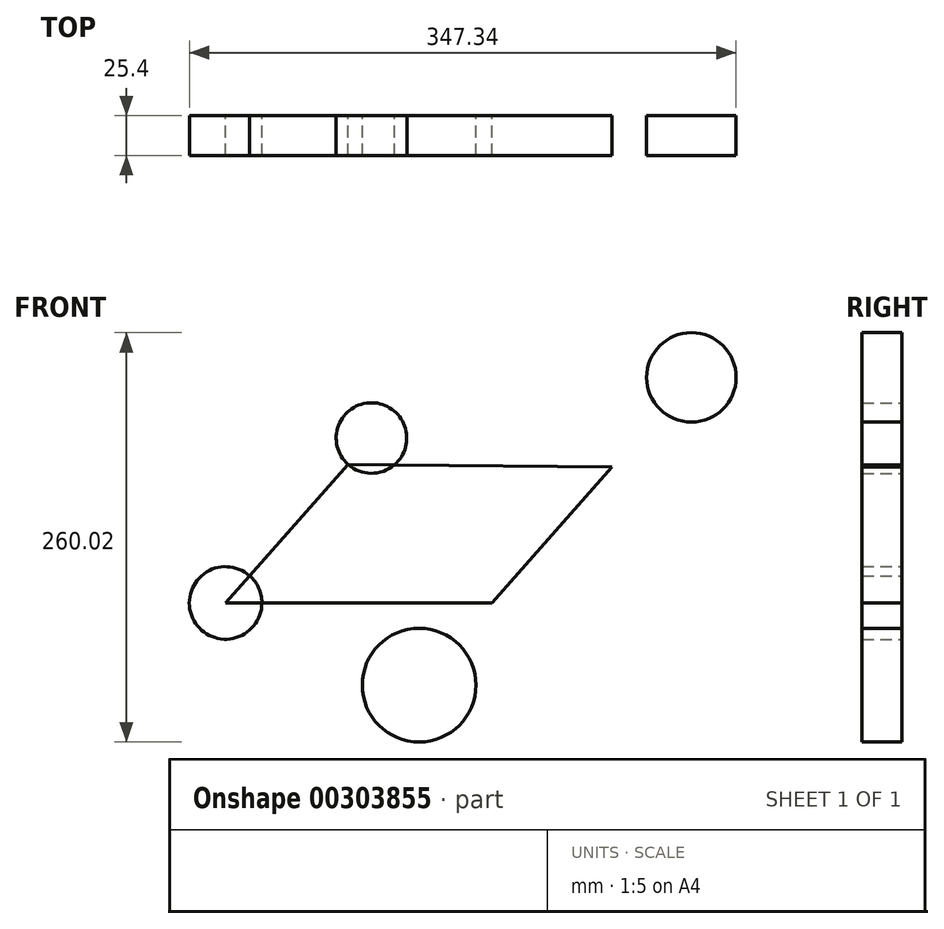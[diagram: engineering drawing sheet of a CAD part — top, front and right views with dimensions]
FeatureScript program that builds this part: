
annotation { "Feature Type Name" : "Feature", "Feature Type Description" : "" }
export const myFeature = defineFeature(function(context is Context, id is Id, definition is map)
    precondition{}
    {
        {
            var Q0;
            Q0=qCreatedBy(makeId("Front.planeOp"),FACE);
            var sketch = newSketch(context, id + "F0", { "sketchPlane" : qUnion([Q0])});
            skLineSegment(sketch, "E0", {"start": v(-129.95, -28.94) * mm, "end": v(-37.28, 75.8) * mm});
            skCircle(sketch, "E1", {"center": v(-37.28, 75.8) * mm, "radius": 22.41 * mm});
            skCircle(sketch, "E2", {"center": v(-129.95, -28.94) * mm, "radius": 23.04 * mm});
            skLineSegment(sketch, "E3", {"start": v(-129.95, -28.94) * mm, "end": v(39.16, -28.94) * mm});
            skLineSegment(sketch, "E4", {"start": v(39.16, -28.94) * mm, "end": v(115.44, 57.28) * mm});
            skLineSegment(sketch, "E5", {"start": v(115.44, 57.28) * mm, "end": v(-52.13, 59.02) * mm});
            skLineSegment(sketch, "E6", {"start": v(115.44, 57.28) * mm, "end": v(-7.02, -81.15) * mm});
            skLineSegment(sketch, "E7", {"start": v(-7.02, -81.15) * mm, "end": v(115.44, 57.28) * mm});
            skLineSegment(sketch, "E8", {"start": v(115.44, 57.28) * mm, "end": v(165.93, 114.35) * mm});
            skCircle(sketch, "E9", {"center": v(-7.02, -81.15) * mm, "radius": 36.1 * mm});
            skCircle(sketch, "E10", {"center": v(165.93, 114.35) * mm, "radius": 28.42 * mm});
            skSolve(sketch);
        }
        {
            var Q0;
            {var subQ0=sQuery(id+"F0.wireOp",EDGE,"E3");var subQ1=sQuery(id+"F0.wireOp",EDGE,"E0");var subQ2=makeQuery(id+"F0.imprint","INTERSECT",VERTEX,{"derivedFrom":[subQ1,subQ0]});Q0=makeQuery(id+"F0.imprint","IMPRINT",FACE,{"disambiguationData":[TD([[makeQuery(id+"F0.imprint","IMPRINT",EDGE,{"disambiguationData":[TD([[subQ2,-1.0]])],"derivedFrom":subQ1}),1.0]])]});}
            var Q1;
            Q1=makeQuery(id+"F0.imprint","IMPRINT",FACE,{"disambiguationData":[TD([[makeQuery(id+"F0.imprint","IMPRINT",EDGE,{"derivedFrom":sQuery(id+"F0.wireOp",EDGE,"E10")}),1.0]])]});
            var Q2;
            {var subQ0=sQuery(id+"F0.wireOp",EDGE,"E5");var subQ1=sQuery(id+"F0.wireOp",EDGE,"E1");var subQ3=makeQuery(id+"F0.imprint","INTERSECT",VERTEX,{"derivedFrom":[subQ1,subQ0]});Q2=makeQuery(id+"F0.imprint","IMPRINT",FACE,{"disambiguationData":[TD([[makeQuery(id+"F0.imprint","IMPRINT",EDGE,{"disambiguationData":[TD([[subQ3,-1.0]])],"derivedFrom":subQ1}),1.0]])]});}
            var Q3;
            {var subQ0=sQuery(id+"F0.wireOp",EDGE,"E2");var subQ1=sQuery(id+"F0.wireOp",EDGE,"E0");var subQ2=makeQuery(id+"F0.imprint","INTERSECT",VERTEX,{"derivedFrom":[subQ1,subQ0]});Q3=makeQuery(id+"F0.imprint","IMPRINT",FACE,{"disambiguationData":[TD([[makeQuery(id+"F0.imprint","IMPRINT",EDGE,{"disambiguationData":[TD([[subQ2,1.0]])],"derivedFrom":subQ0}),-1.0]])]});}
            var Q4;
            Q4=makeQuery(id+"F0.imprint","IMPRINT",FACE,{"disambiguationData":[TD([[makeQuery(id+"F0.imprint","IMPRINT",EDGE,{"derivedFrom":sQuery(id+"F0.wireOp",EDGE,"E9")}),1.0]])]});
            extrude(context, id + "F1", {"entities" : qUnion([Q0, Q1, Q2, Q3, Q4]), "depth" : 25.4 * mm});
        }
    });
